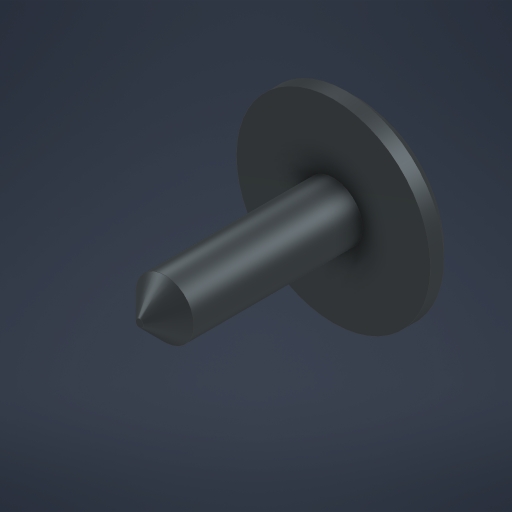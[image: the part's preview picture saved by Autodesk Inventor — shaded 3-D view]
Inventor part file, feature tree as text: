
AUTODESK INVENTOR PART (.ipt)
format: ipt  version: 2023 (Build 270158000, 158)  size: 294,400 bytes
history: native  units: mm
features: chamfer x5, extrude x3, sketch x3, fillet x1
ambient origin geometry x8: Origin, YZ Plane, XZ Plane, XY Plane, X Axis, Y Axis, Z Axis, Center Point
bodies: Solid1 (feature_tree)
feature tree (12):
  extrude  "Extrusion1"  Depth=2.0mm TaperAngle=0.0deg
  extrude  "Extrusion2"  Depth=10.0mm TaperAngle=0.0deg
  chamfer  "Chamfer1"  Distance=1.3mm Angle=45.0deg
  chamfer  "Chamfer2"  Distance=1.3mm Angle=45.0deg
  fillet  "Fillet1"  Radius=3.0mm
  extrude  "Extrusion3"  Depth=1.0mm
  chamfer  "Chamfer3"  Distance=1.0mm
  chamfer  "Chamfer4"  Distance=0.5mm Angle=45.0deg
  chamfer  "Chamfer5"  Distance=0.5mm Angle=45.0deg
  sketch  "Sketch1"  dims[d0=10.0mm d1=2.0mm d2=0.0mm]
  sketch  "Sketch2"  dims[d3=3.0mm d4=10.0mm d5=0.0mm d6=1.3mm d7=2.0mm d8=45.0deg d9=1.3mm d10=2.0mm d11=45.0deg d12=3.0mm]
  sketch  "Sketch3"  dims[d15=6.0mm d16=1.0mm d17=1.0mm d18=0.0mm d19=0.5mm d20=2.0mm d21=45.0deg d22=0.5mm d23=2.0mm d24=45.0deg d25=0.5mm d26=2.0mm d27=45.0deg]
